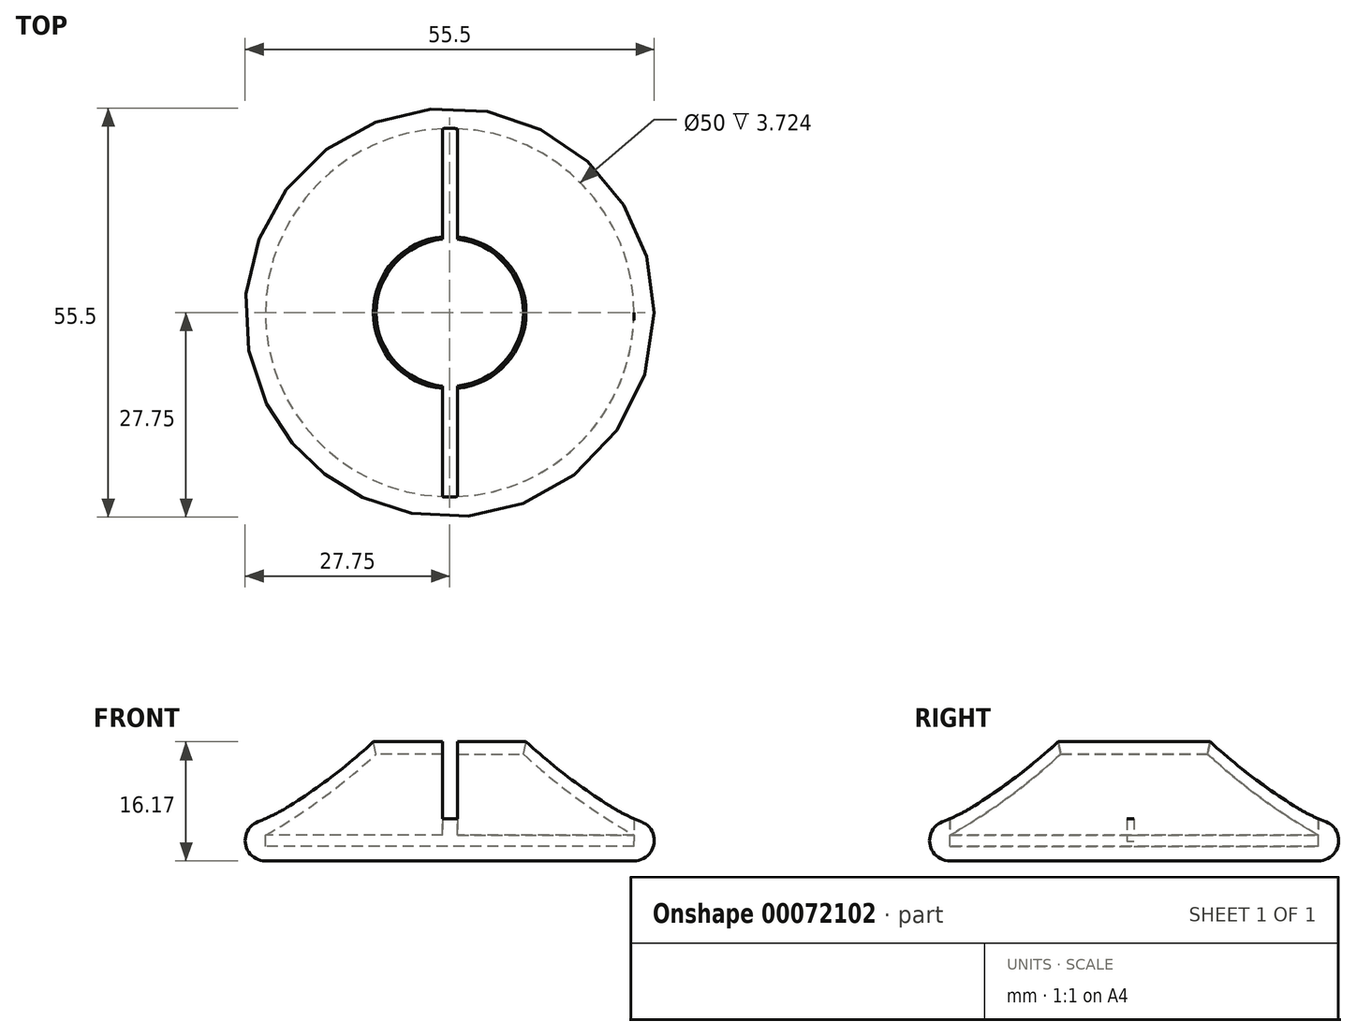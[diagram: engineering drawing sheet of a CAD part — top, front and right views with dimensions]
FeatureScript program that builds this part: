
annotation { "Feature Type Name" : "Feature", "Feature Type Description" : "" }
export const myFeature = defineFeature(function(context is Context, id is Id, definition is map)
    precondition{}
    {
        {
            var Q0;
            Q0=qCreatedBy(makeId("Front.planeOp"),FACE);
            var sketch = newSketch(context, id + "F0", { "sketchPlane" : qUnion([Q0])});
            skLineSegment(sketch, "E0", {"start": v(0, 0) * mm, "end": v(-14, 0) * mm, "construction": true});
            skLineSegment(sketch, "E1", {"start": v(-7, 0) * mm, "end": v(-7, -3.4) * mm, "construction": true});
            skLineSegment(sketch, "E2", {"start": v(18, -10) * mm, "end": v(18, -11.5) * mm});
            skLineSegment(sketch, "E3", {"start": v(18, -11.5) * mm, "end": v(-7, -11.5) * mm});
            skLineSegment(sketch, "E4", {"start": v(-7, -11.5) * mm, "end": v(-7, -13.5) * mm});
            skLineSegment(sketch, "E5", {"start": v(-7, -13.5) * mm, "end": v(18, -13.5) * mm});
            skArc(sketch, "E6", {"start": v(18, -13.5) * mm, "mid": v(20.75, -10.75) * mm, "end": v(18, -8) * mm});
            skArc(sketch, "E7", {"start": v(3, 1) * mm, "mid": v(10.18, -4.94) * mm, "end": v(18, -10) * mm});
            skLineSegment(sketch, "E8", {"start": v(3, 1) * mm, "end": v(3, 3) * mm});
            skArc(sketch, "E9", {"start": v(3, 3) * mm, "mid": v(10.18, -2.94) * mm, "end": v(18, -8) * mm});
            skSolve(sketch);
        }
        {
            var Q0;
            {var subQ4=sQuery(id+"F0.wireOp",EDGE,"E2");Q0=makeQuery(id+"F0.imprint","IMPRINT",FACE,{"disambiguationData":[TD([[makeQuery(id+"F0.imprint","IMPRINT",EDGE,{"derivedFrom":subQ4}),1.0]])]});}
            var Q1;
            Q1=sQuery(id+"F0.wireOp",EDGE,"E1");
            revolve(context, id + "F1", {"entities" : qUnion([Q0]), "axis" : qUnion([Q1]), "revolveType" : RevolveType.ONE_DIRECTION, "angle" : 360 * degree});
        }
        {
            var Q0;
            Q0=makeQuery(id+"F1.opRevolve","SWEPT_EDGE",EDGE,{"disambiguationData":[OSD([sQuery(id+"F0.wireOp",EDGE,"E8"),sQuery(id+"F0.wireOp",EDGE,"E9")])]});
            chamfer(context, id + "F2", {"entities" : qUnion([Q0]), "chamferType" : ChamferType.TWO_OFFSETS, "width1" : .5 * mm, "oppositeDirection" : true, "width2" : 2 * mm, "tangentPropagation" : true});
        }
        {
            var Q0;
            Q0=makeQuery(id+"F1.opRevolve","SWEPT_EDGE",EDGE,{"disambiguationData":[OSD([sQuery(id+"F0.wireOp",EDGE,"E6"),sQuery(id+"F0.wireOp",EDGE,"E9")])]});
            fillet(context, id + "F3", {"entities" : qUnion([Q0]), "radius" : 25 * mm, "tangentPropagation" : true, "allowEdgeOverflow" : false});
        }
        {
            var Q0;
            Q0=makeQuery(id+"F1.opRevolve","SWEPT_FACE",FACE,{"disambiguationData":[OSD([sQuery(id+"F0.wireOp",EDGE,"E5")])]});
            var sketch = newSketch(context, id + "F4", { "sketchPlane" : qUnion([Q0])});
            skLineSegment(sketch, "E10", {"start": v(-5.95, -25) * mm, "end": v(-5.95, 25) * mm});
            skLineSegment(sketch, "E11", {"start": v(-5.95, 25) * mm, "end": v(-7.95, 25) * mm});
            skLineSegment(sketch, "E12", {"start": v(-7.95, 25) * mm, "end": v(-7.95, -25) * mm});
            skLineSegment(sketch, "E13", {"start": v(-5.95, -25) * mm, "end": v(-7.95, -25) * mm});
            skLineSegment(sketch, "E14", {"start": v(-6.95, -25) * mm, "end": v(18, 0) * mm, "construction": true});
            skLineSegment(sketch, "E15", {"start": v(18, 0) * mm, "end": v(-7.05, 25) * mm, "construction": true});
            skLineSegment(sketch, "E16", {"start": v(-7.05, 25) * mm, "end": v(-32, 0) * mm, "construction": true});
            skLineSegment(sketch, "E17", {"start": v(-32, 0) * mm, "end": v(-6.95, -25) * mm, "construction": true});
            skLineSegment(sketch, "E18", {"start": v(-6.95, -25) * mm, "end": v(-6.95, -25) * mm});
            skLineSegment(sketch, "E19.bottom", {"start": v(18, 1) * mm, "end": v(-5.95, 1) * mm});
            skLineSegment(sketch, "E19.top", {"start": v(18, -1) * mm, "end": v(-5.95, -1) * mm});
            skLineSegment(sketch, "E19.left", {"start": v(18, 1) * mm, "end": v(18, -1) * mm});
            skLineSegment(sketch, "E19.right", {"start": v(-5.95, 1) * mm, "end": v(-5.95, -1) * mm});
            skLineSegment(sketch, "E20", {"start": v(18, 0) * mm, "end": v(18, 0) * mm});
            skSolve(sketch);
        }
        {
            var Q0;
            Q0=makeQuery(id+"F4.imprint","IMPRINT",FACE,{"disambiguationData":[TD([[makeQuery(id+"F4.imprint","IMPRINT",EDGE,{"derivedFrom":sQuery(id+"F4.wireOp",EDGE,"E10")}),1.0]])]});
            var Q1;
            Q1=makeQuery(id+"F4.imprint","IMPRINT",FACE,{"disambiguationData":[TD([[makeQuery(id+"F4.imprint","IMPRINT",EDGE,{"derivedFrom":sQuery(id+"F4.wireOp",EDGE,"E19.bottom")}),1.0]])]});
            var Q2;
            {var subQ0=sQuery(id+"F4.wireOp",EDGE,"E19.right");Q2=makeQuery(id+"F4.imprint","IMPRINT",FACE,{"disambiguationData":[TD([[makeQuery(id+"F4.imprint","IMPRINT",EDGE,{"derivedFrom":subQ0}),1.0]])]});}
            extrude(context, id + "F5", {"entities" : qUnion([Q0, Q1, Q2]), "operationType" : NewBodyOperationType.REMOVE, "oppositeDirection" : true, "depth" : 25 * mm, "hasSecondDirection" : true, "secondDirectionOppositeDirection" : true, "secondDirectionDepth" : 2.7 * mm});
        }
    });
